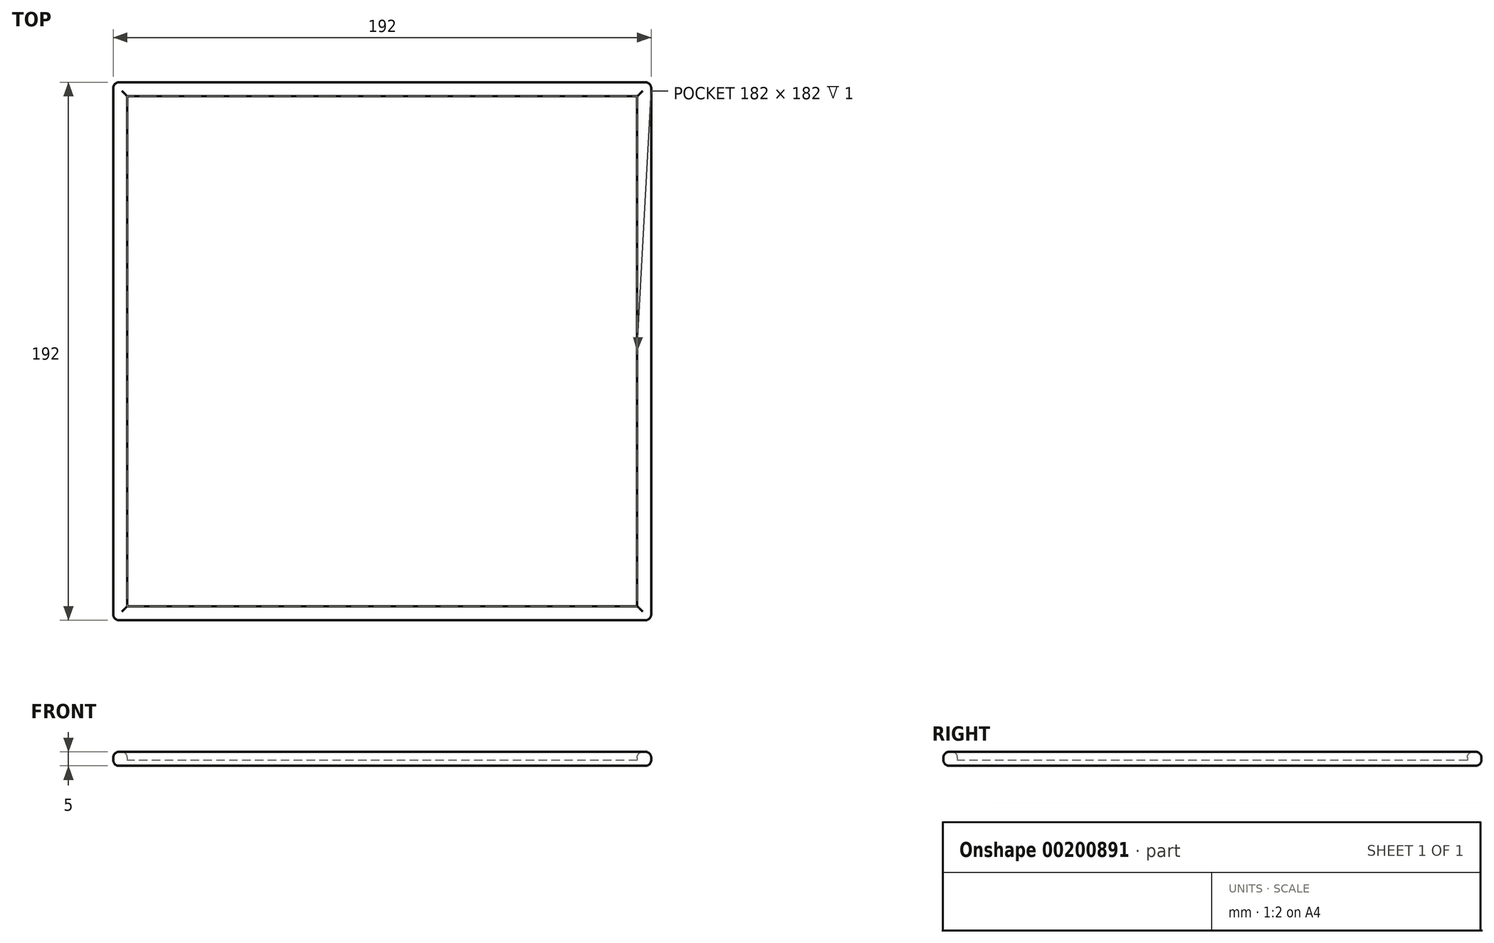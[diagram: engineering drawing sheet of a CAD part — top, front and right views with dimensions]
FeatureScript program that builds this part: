
annotation { "Feature Type Name" : "Feature", "Feature Type Description" : "" }
export const myFeature = defineFeature(function(context is Context, id is Id, definition is map)
    precondition{}
    {
        {
            var Q0;
            Q0=qCreatedBy(makeId("Top.planeOp"),FACE);
            var sketch = newSketch(context, id + "F0", { "sketchPlane" : qUnion([Q0])});
            skLineSegment(sketch, "E0.bottom", {"start": v(96, 96) * mm, "end": v(-96, 96) * mm});
            skLineSegment(sketch, "E0.top", {"start": v(96, -96) * mm, "end": v(-96, -96) * mm});
            skLineSegment(sketch, "E0.left", {"start": v(96, 96) * mm, "end": v(96, -96) * mm});
            skLineSegment(sketch, "E0.right", {"start": v(-96, 96) * mm, "end": v(-96, -96) * mm});
            skPoint(sketch, "E0.middle", {"position": v(0, 0) * mm});
            skLineSegment(sketch, "E1.bottom", {"start": v(91, 91) * mm, "end": v(-91, 91) * mm});
            skLineSegment(sketch, "E1.top", {"start": v(91, -91) * mm, "end": v(-91, -91) * mm});
            skLineSegment(sketch, "E1.left", {"start": v(91, 91) * mm, "end": v(91, -91) * mm});
            skLineSegment(sketch, "E1.right", {"start": v(-91, 91) * mm, "end": v(-91, -91) * mm});
            skSolve(sketch);
        }
        {
            var Q0;
            Q0=makeQuery(id+"F0.imprint","IMPRINT",FACE,{"disambiguationData":[TD([[makeQuery(id+"F0.imprint","IMPRINT",EDGE,{"derivedFrom":sQuery(id+"F0.wireOp",EDGE,"E1.bottom")}),1.0]])]});
            extrude(context, id + "F1", {"entities" : qUnion([Q0]), "depth" : 2 * mm});
        }
        {
            var Q0;
            Q0 = qSketchRegion(id + "F0", true);
            extrude(context, id + "F2", {"entities" : qUnion([Q0]), "operationType" : NewBodyOperationType.ADD, "depth" : 5 * mm});
        }
        {
            var Q0;
            Q0=makeQuery(id+"F2.opExtrude","SWEPT_FACE",FACE,{"disambiguationData":[OSD([sQuery(id+"F0.wireOp",EDGE,"E0.top")])]});
            var Q1;
            Q1=makeQuery(id+"F2.opExtrude","SWEPT_FACE",FACE,{"disambiguationData":[OSD([sQuery(id+"F0.wireOp",EDGE,"E0.left")])]});
            var Q2;
            Q2=makeQuery(id+"F2.opExtrude","SWEPT_FACE",FACE,{"disambiguationData":[OSD([sQuery(id+"F0.wireOp",EDGE,"E0.bottom")])]});
            var Q3;
            Q3=makeQuery(id+"F2.opExtrude","SWEPT_FACE",FACE,{"disambiguationData":[OSD([sQuery(id+"F0.wireOp",EDGE,"E0.right")])]});
            var Q4;
            Q4=makeQuery(id+"F2.opExtrude","CAP_FACE",FACE,{"disambiguationData":[OSD([sQuery(id+"F0.wireOp",EDGE,"E0.bottom"),sQuery(id+"F0.wireOp",EDGE,"E0.top"),sQuery(id+"F0.wireOp",EDGE,"E0.left"),sQuery(id+"F0.wireOp",EDGE,"E0.right"),sQuery(id+"F0.wireOp",EDGE,"E1.bottom"),sQuery(id+"F0.wireOp",EDGE,"E1.top"),sQuery(id+"F0.wireOp",EDGE,"E1.left"),sQuery(id+"F0.wireOp",EDGE,"E1.right")])],"isStart":false});
            fillet(context, id + "F3", {"entities" : qUnion([Q0, Q1, Q2, Q3, Q4]), "radius" : 2 * mm, "tangentPropagation" : true, "allowEdgeOverflow" : false});
        }
    });
